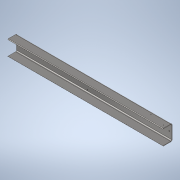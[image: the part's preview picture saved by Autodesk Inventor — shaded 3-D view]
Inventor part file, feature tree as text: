
AUTODESK INVENTOR PART (.ipt)
format: ipt  version: 2020 (Build 240168000, 168)  size: 166,912 bytes
history: native  units: mm
features: sheet_metal_op x4, sketch x4, other x4, projected_geometry x3, hole x2, chamfer x1, reference x1
ambient origin geometry x8: Origin, YZ Plane, XZ Plane, XY Plane, X Axis, Y Axis, Z Axis, Center Point
bodies: Solid1 (feature_tree)
feature tree (19):
  sheet_metal_op  "Face1"
  sheet_metal_op  "Flange1"
  chamfer  "Chamfer1"  Distance=5.0mm
  hole  "Hole1"  [1 undecoded]
  hole  "Hole2"  [1 undecoded]
  sketch  "Sketch1"  dims[d0=3000.0mm]
  other  "Plate1"
  sketch  "Sketch2"  dims[d1=280.0mm]
  other  "Plate2"
  sheet_metal_op  "Bend1"
  sheet_metal_op  "Corner1"
  sketch  "Sketch3"  dims[d2=10.0mm]
  projected_geometry  "Projected Loop1"
  reference  "Reference1"
  sketch  "Sketch4"  dims[d3=10.0mm d4=5.0mm d5=20.0mm d6=10.0mm d7=180.0mm d8=90.0deg d9=20.0mm d10=40.0mm d11=10.0mm d12=10.0mm d13=9.0mm d14=2.0mm d15=45.0deg d16=45.0mm d17=95.0mm d18=105.0mm d19=130.0mm d20=100.0mm d22=18.631mm d23=41.91mm d24=4.0mm d25=2.0mm d26=90.0deg d27=50.41mm d28=20.594885mm d29=100.0mm d30=50.0mm d31=116.0mm d32=351.0mm d33=60.0mm d34=8.376mm d35=10.0mm d36=4.0mm d37=2.0mm d38=90.0deg d39=27.3mm d40=20.594885mm]
  projected_geometry  "Projected Loop2"
  projected_geometry  "Projected Loop3"
  other  "SlipersLåda 211018000.iam"
  other  "SlipersLåda 211018012:1"
note: 2 required parameter values undecoded (feature->parameter linkage not recoverable at this tier; creation-order binding heuristic only, values carry confidence <= 0.55)
